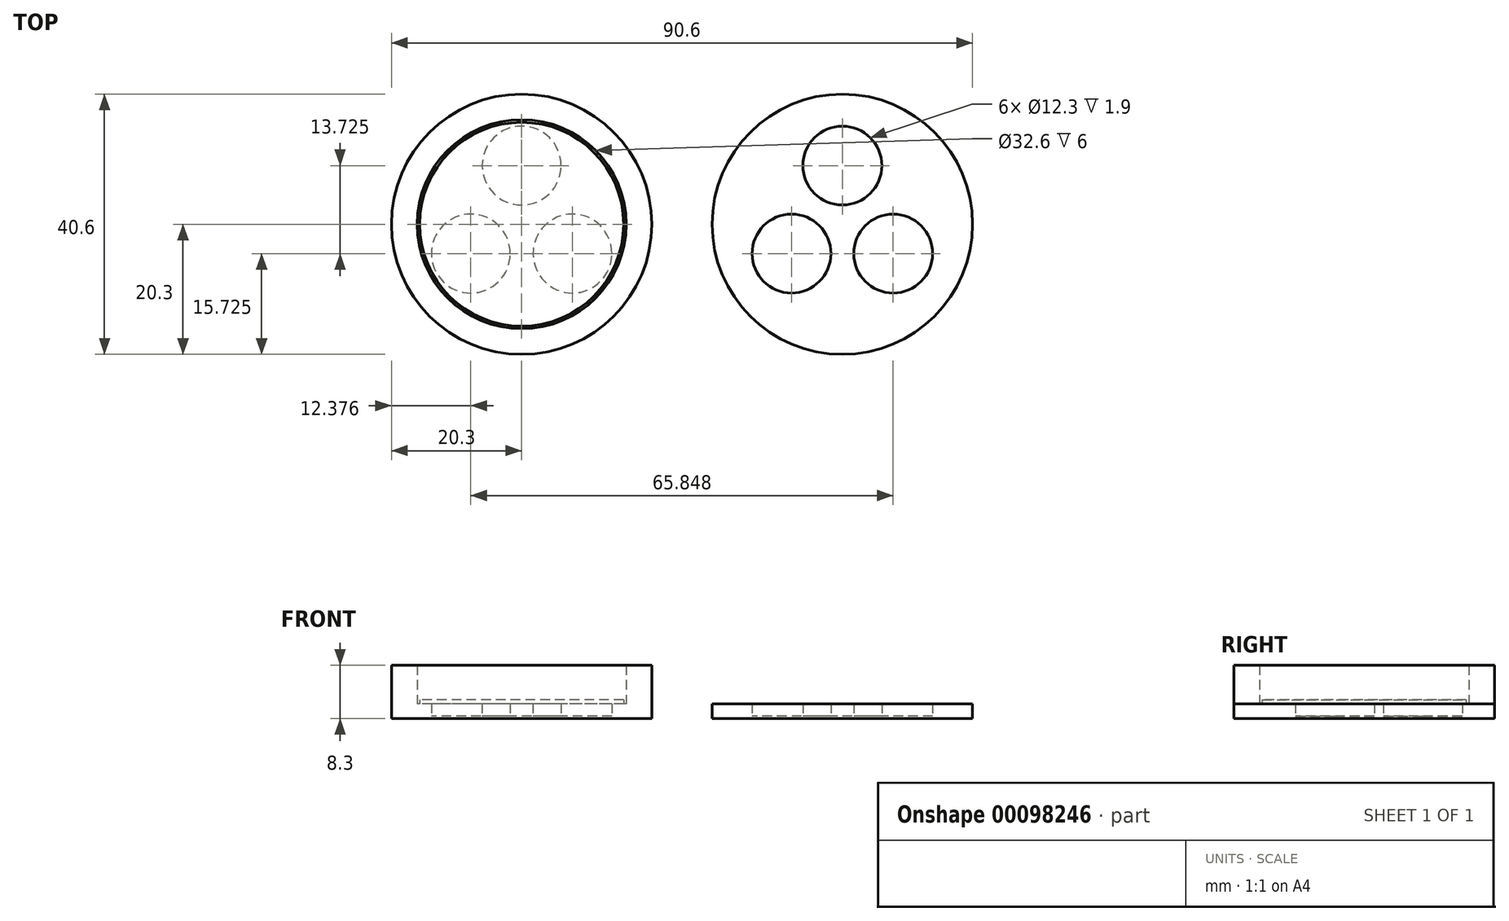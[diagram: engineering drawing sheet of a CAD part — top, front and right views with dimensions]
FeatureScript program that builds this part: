
annotation { "Feature Type Name" : "Feature", "Feature Type Description" : "" }
export const myFeature = defineFeature(function(context is Context, id is Id, definition is map)
    precondition{}
    {
        {
            var Q0;
            Q0=qCreatedBy(makeId("Top.planeOp"),FACE);
            var sketch = newSketch(context, id + "F0", { "sketchPlane" : qUnion([Q0])});
            skCircle(sketch, "E0", {"center": v(0, 0) * mm, "radius": 15.3 * mm});
            skCircle(sketch, "E1", {"center": v(0, 9.15) * mm, "radius": 6.15 * mm});
            skCircle(sketch, "E2.1.0", {"center": v(-7.92, -4.57) * mm, "radius": 6.15 * mm});
            skCircle(sketch, "E2.2.0", {"center": v(7.92, -4.57) * mm, "radius": 6.15 * mm});
            skCircle(sketch, "E3", {"center": v(0, 0) * mm, "radius": 20.3 * mm});
            skSolve(sketch);
        }
        {
            var Q0;
            Q0 = qSketchRegion(id + "F0", true);
            var Q1;
            {var subQ0=sQuery(id+"F0.wireOp",EDGE,"E1");Q1=makeQuery(id+"F0.imprint","IMPRINT",FACE,{"disambiguationData":[TD([[makeQuery(id+"F0.imprint","IMPRINT",EDGE,{"derivedFrom":subQ0}),-1.0]])]});}
            extrude(context, id + "F1", {"entities" : qUnion([Q0, Q1]), "depth" : 1.9 * mm});
        }
        {
            var Q0;
            Q0=makeQuery(id+"F1.opExtrude","CAP_FACE",FACE,{"disambiguationData":[OSD([sQuery(id+"F0.wireOp",EDGE,"E1"),sQuery(id+"F0.wireOp",EDGE,"E2.1.0"),sQuery(id+"F0.wireOp",EDGE,"E2.2.0"),sQuery(id+"F0.wireOp",EDGE,"E3")])],"isStart":true});
            var sketch = newSketch(context, id + "F2", { "sketchPlane" : qUnion([Q0])});
            skCircle(sketch, "E4.0", {"center": v(0, 0) * mm, "radius": 20.3 * mm});
            skSolve(sketch);
        }
        {
            var Q0;
            Q0 = qSketchRegion(id + "F2", true);
            extrude(context, id + "F3", {"entities" : qUnion([Q0]), "operationType" : NewBodyOperationType.ADD, "depth" : 0.4 * mm});
        }
        {
            var Q0;
            Q0=makeQuery(id+"F1.opExtrude","SWEPT_BODY",BODY,{"disambiguationData":[OSD([sQuery(id+"F0.wireOp",EDGE,"E1"),sQuery(id+"F0.wireOp",EDGE,"E2.1.0"),sQuery(id+"F0.wireOp",EDGE,"E2.2.0"),sQuery(id+"F0.wireOp",EDGE,"E3")])]});
            transform(context, id + "F4", {"entities" : qUnion([Q0]), "transformType" : TransformType.TRANSLATION_3D, "dx" : 50 * mm, "dy" : 0 * mm, "dz" : 0 * mm, "makeCopy" : true});
        }
        {
            var Q0;
            Q0=makeQuery(id+"F1.opExtrude","CAP_FACE",FACE,{"disambiguationData":[OSD([sQuery(id+"F0.wireOp",EDGE,"E1"),sQuery(id+"F0.wireOp",EDGE,"E2.1.0"),sQuery(id+"F0.wireOp",EDGE,"E2.2.0"),sQuery(id+"F0.wireOp",EDGE,"E3")])],"isStart":false});
            var sketch = newSketch(context, id + "F5", { "sketchPlane" : qUnion([Q0])});
            skCircle(sketch, "E5", {"center": v(0, 0) * mm, "radius": 16.3 * mm});
            skCircle(sketch, "E6.0", {"center": v(0, 0) * mm, "radius": 20.3 * mm});
            skSolve(sketch);
        }
        {
            var Q0;
            Q0=makeQuery(id+"F5.imprint","IMPRINT",FACE,{"disambiguationData":[TD([[makeQuery(id+"F5.imprint","IMPRINT",EDGE,{"derivedFrom":sQuery(id+"F5.wireOp",EDGE,"E5")}),-1.0]])]});
            extrude(context, id + "F6", {"entities" : qUnion([Q0]), "operationType" : NewBodyOperationType.ADD, "depth" : 6 * mm});
        }
        {
            var Q0;
            Q0=makeQuery(id+"F1.opExtrude","CAP_FACE",FACE,{"disambiguationData":[OSD([sQuery(id+"F0.wireOp",EDGE,"E1"),sQuery(id+"F0.wireOp",EDGE,"E2.1.0"),sQuery(id+"F0.wireOp",EDGE,"E2.2.0"),sQuery(id+"F0.wireOp",EDGE,"E3")])],"isStart":false});
            var sketch = newSketch(context, id + "F7", { "sketchPlane" : qUnion([Q0])});
            skCircle(sketch, "E7.0", {"center": v(0, 0) * mm, "radius": 16.3 * mm});
            skCircle(sketch, "E8", {"center": v(0, 0) * mm, "radius": 15.9 * mm});
            skSolve(sketch);
        }
        {
            var Q0;
            Q0=makeQuery(id+"F7.imprint","IMPRINT",FACE,{"disambiguationData":[TD([[makeQuery(id+"F7.imprint","IMPRINT",EDGE,{"derivedFrom":sQuery(id+"F7.wireOp",EDGE,"E8")}),1.0]])]});
            var Q1;
            Q1=makeQuery(id+"F7.imprint","IMPRINT",FACE,{"disambiguationData":[TD([[makeQuery(id+"F7.imprint","IMPRINT",EDGE,{"derivedFrom":makeQuery(id+"F1.opExtrude","CAP_EDGE",EDGE,{"disambiguationData":[OSD([sQuery(id+"F0.wireOp",EDGE,"E2.1.0")])],"isStart":false})}),1.0]])]});
            var Q2;
            Q2=makeQuery(id+"F7.imprint","IMPRINT",FACE,{"disambiguationData":[TD([[makeQuery(id+"F7.imprint","IMPRINT",EDGE,{"derivedFrom":makeQuery(id+"F1.opExtrude","CAP_EDGE",EDGE,{"disambiguationData":[OSD([sQuery(id+"F0.wireOp",EDGE,"E2.2.0")])],"isStart":false})}),1.0]])]});
            var Q3;
            Q3=makeQuery(id+"F7.imprint","IMPRINT",FACE,{"disambiguationData":[TD([[makeQuery(id+"F7.imprint","IMPRINT",EDGE,{"derivedFrom":makeQuery(id+"F1.opExtrude","CAP_EDGE",EDGE,{"disambiguationData":[OSD([sQuery(id+"F0.wireOp",EDGE,"E1")])],"isStart":false})}),1.0]])]});
            extrude(context, id + "F8", {"entities" : qUnion([Q0, Q1, Q2, Q3]), "depth" : 0.6 * mm});
        }
    });
